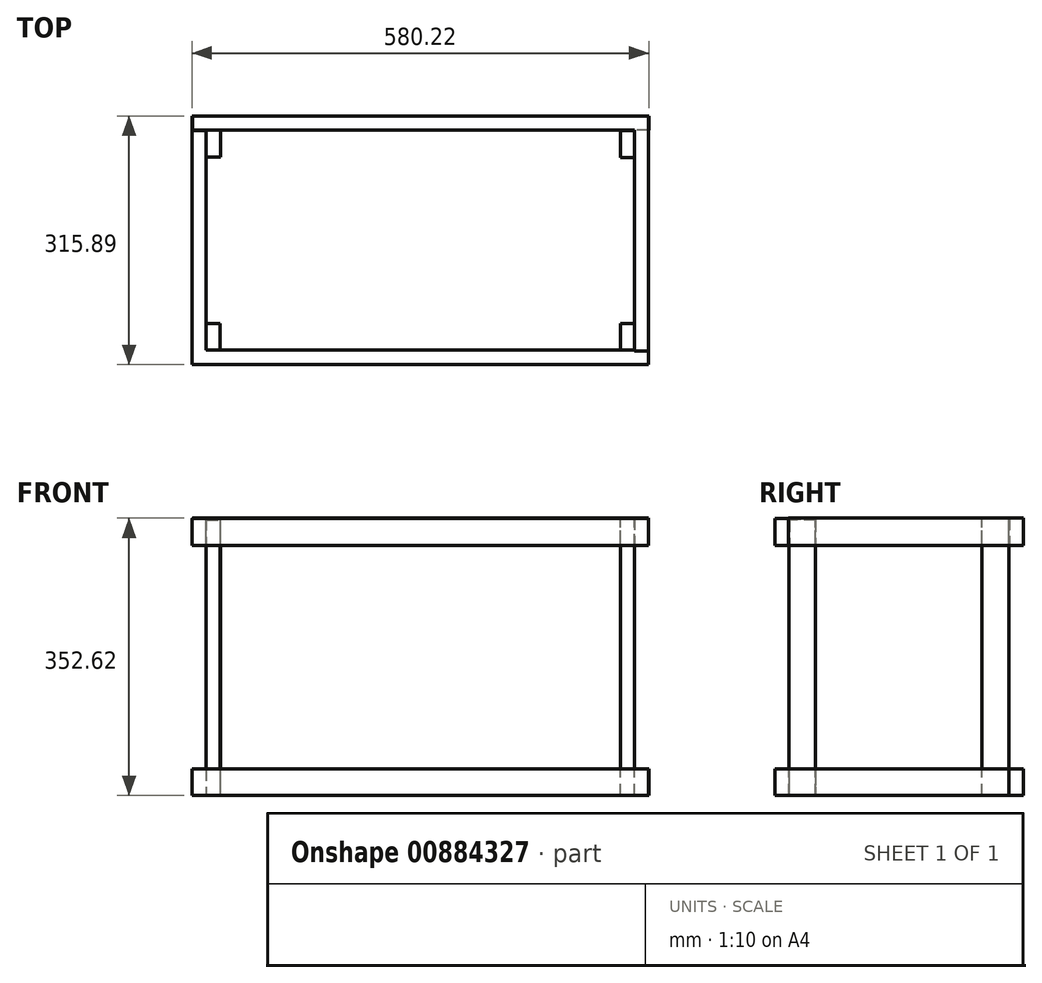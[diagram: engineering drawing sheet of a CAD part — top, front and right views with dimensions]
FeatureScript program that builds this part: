
annotation { "Feature Type Name" : "Feature", "Feature Type Description" : "" }
export const myFeature = defineFeature(function(context is Context, id is Id, definition is map)
    precondition{}
    {
        {
            var Q0;
            Q0=qCreatedBy(makeId("Top.planeOp"),FACE);
            var sketch = newSketch(context, id + "F0", { "sketchPlane" : qUnion([Q0])});
            skLineSegment(sketch, "E0.bottom", {"start": v(0, 0) * mm, "end": v(-18, 0) * mm});
            skLineSegment(sketch, "E0.top", {"start": v(0, -33.75) * mm, "end": v(-18, -33.75) * mm});
            skLineSegment(sketch, "E0.left", {"start": v(0, 0) * mm, "end": v(0, -33.75) * mm});
            skLineSegment(sketch, "E0.right", {"start": v(-18, 0) * mm, "end": v(-18, -33.75) * mm});
            skSolve(sketch);
        }
        {
            var Q0;
            Q0 = qSketchRegion(id + "F0", true);
            extrude(context, id + "F1", {"entities" : qUnion([Q0]), "depth" : 350 * mm, "offsetDistance" : 25.4 * mm});
        }
        {
            var Q0;
            Q0=qCreatedBy(makeId("Top.planeOp"),FACE);
            var sketch = newSketch(context, id + "F2", { "sketchPlane" : qUnion([Q0])});
            skLineSegment(sketch, "E1.bottom", {"start": v(-17.7, -33.83) * mm, "end": v(-35.69, -33.83) * mm});
            skLineSegment(sketch, "E1.top", {"start": v(-17.7, 245.87) * mm, "end": v(-35.69, 245.87) * mm});
            skLineSegment(sketch, "E1.left", {"start": v(-17.7, -33.83) * mm, "end": v(-17.7, 245.87) * mm});
            skLineSegment(sketch, "E1.right", {"start": v(-35.69, -33.83) * mm, "end": v(-35.69, 245.87) * mm});
            skSolve(sketch);
        }
        {
            var Q0;
            Q0 = qSketchRegion(id + "F2", true);
            extrude(context, id + "F3", {"entities" : qUnion([Q0]), "operationType" : NewBodyOperationType.ADD, "depth" : 33.78 * mm, "offsetDistance" : 25.4 * mm});
        }
        {
            var Q0;
            Q0=makeQuery(id+"F3.opExtrude","SWEPT_FACE",FACE,{"disambiguationData":[OSD([sQuery(id+"F2.wireOp",EDGE,"E1.bottom")])]});
            var sketch = newSketch(context, id + "F4", { "sketchPlane" : qUnion([Q0])});
            skPoint(sketch, "E2.oppositeSnap0", {"position": v(-26.7, 33.78) * mm});
            skLineSegment(sketch, "E2.bottom", {"start": v(-35.69, 0) * mm, "end": v(544.25, 0) * mm});
            skLineSegment(sketch, "E2.top", {"start": v(-35.69, 33.78) * mm, "end": v(544.25, 33.78) * mm});
            skLineSegment(sketch, "E2.left", {"start": v(-35.69, 0) * mm, "end": v(-35.69, 33.78) * mm});
            skLineSegment(sketch, "E2.right", {"start": v(544.25, 0) * mm, "end": v(544.25, 33.78) * mm});
            skSolve(sketch);
        }
        {
            var Q0;
            Q0 = qSketchRegion(id + "F4", true);
            extrude(context, id + "F5", {"entities" : qUnion([Q0]), "operationType" : NewBodyOperationType.ADD, "depth" : 18.03 * mm, "offsetDistance" : 25.4 * mm});
        }
        {
            var Q0;
            Q0=makeQuery(id+"F5.opExtrude","CAP_FACE",FACE,{"disambiguationData":[OSD([sQuery(id+"F4.wireOp",EDGE,"E2.bottom"),sQuery(id+"F4.wireOp",EDGE,"E2.top"),sQuery(id+"F4.wireOp",EDGE,"E2.left"),sQuery(id+"F4.wireOp",EDGE,"E2.right")])],"isStart":true});
            var sketch = newSketch(context, id + "F6", { "sketchPlane" : qUnion([Q0])});
            skLineSegment(sketch, "E3.bottom", {"start": v(-544.25, 0) * mm, "end": v(-526.26, 0) * mm});
            skLineSegment(sketch, "E3.top", {"start": v(-544.25, 33.78) * mm, "end": v(-526.26, 33.78) * mm});
            skLineSegment(sketch, "E3.left", {"start": v(-544.25, 0) * mm, "end": v(-544.25, 33.78) * mm});
            skLineSegment(sketch, "E3.right", {"start": v(-526.26, 0) * mm, "end": v(-526.26, 33.78) * mm});
            skSolve(sketch);
        }
        {
            var Q0;
            Q0=makeQuery(id+"F6.imprint","IMPRINT",FACE,{"disambiguationData":[TD([[makeQuery(id+"F6.imprint","IMPRINT",EDGE,{"derivedFrom":sQuery(id+"F6.wireOp",EDGE,"E3.bottom")}),-1.0]])]});
            extrude(context, id + "F7", {"entities" : qUnion([Q0]), "operationType" : NewBodyOperationType.ADD, "depth" : 279.9 * mm, "offsetDistance" : 25.4 * mm});
        }
        {
            var Q0;
            Q0=makeQuery(id+"F3.opExtrude","SWEPT_FACE",FACE,{"disambiguationData":[OSD([sQuery(id+"F2.wireOp",EDGE,"E1.top")])]});
            var sketch = newSketch(context, id + "F8", { "sketchPlane" : qUnion([Q0])});
            skLineSegment(sketch, "E4.bottom", {"start": v(35.69, 0) * mm, "end": v(-544.48, 0) * mm});
            skLineSegment(sketch, "E4.top", {"start": v(35.69, 33.7) * mm, "end": v(-544.48, 33.7) * mm});
            skLineSegment(sketch, "E4.left", {"start": v(35.69, 0) * mm, "end": v(35.69, 33.7) * mm});
            skLineSegment(sketch, "E4.right", {"start": v(-544.48, 0) * mm, "end": v(-544.48, 33.7) * mm});
            skSolve(sketch);
        }
        {
            var Q0;
            Q0 = qSketchRegion(id + "F8", true);
            extrude(context, id + "F9", {"entities" : qUnion([Q0]), "operationType" : NewBodyOperationType.ADD, "depth" : 18.03 * mm, "offsetDistance" : 25.4 * mm});
        }
        {
            var Q0;
            {var subQ1=sQuery(id+"F2.wireOp",EDGE,"E1.left");var subQ4=sQuery(id+"F0.wireOp",EDGE,"E0.bottom");Q0=makeQuery(id+"F3.boolean.opBoolean","SPLIT",FACE,{"disambiguationData":[TD([makeQuery(id+"F1.opExtrude","SWEPT_FACE",FACE,{"disambiguationData":[OSD([subQ4])]})])],"derivedFrom":makeQuery(id+"F3.opExtrude","SWEPT_FACE",FACE,{"disambiguationData":[OSD([subQ1])]})});}
            var sketch = newSketch(context, id + "F10", { "sketchPlane" : qUnion([Q0])});
            skLineSegment(sketch, "E5.bottom", {"start": v(245.87, 0) * mm, "end": v(211.55, 0) * mm});
            skLineSegment(sketch, "E5.top", {"start": v(245.87, 351.9) * mm, "end": v(211.55, 351.9) * mm});
            skLineSegment(sketch, "E5.left", {"start": v(245.87, 0) * mm, "end": v(245.87, 351.9) * mm});
            skLineSegment(sketch, "E5.right", {"start": v(211.55, 0) * mm, "end": v(211.55, 351.9) * mm});
            skSolve(sketch);
        }
        {
            var Q0;
            Q0 = qSketchRegion(id + "F10", true);
            extrude(context, id + "F11", {"entities" : qUnion([Q0]), "operationType" : NewBodyOperationType.ADD, "depth" : 18.03 * mm, "offsetDistance" : 25.4 * mm});
        }
        {
            var Q0;
            Q0=makeQuery(id+"F7.opExtrude","SWEPT_FACE",FACE,{"disambiguationData":[OSD([sQuery(id+"F6.wireOp",EDGE,"E3.right")])]});
            var sketch = newSketch(context, id + "F12", { "sketchPlane" : qUnion([Q0])});
            skLineSegment(sketch, "E6.bottom", {"start": v(33.83, 0) * mm, "end": v(0, 0) * mm});
            skLineSegment(sketch, "E6.top", {"start": v(33.83, 351.49) * mm, "end": v(0, 351.49) * mm});
            skLineSegment(sketch, "E6.left", {"start": v(33.83, 0) * mm, "end": v(33.83, 351.49) * mm});
            skLineSegment(sketch, "E6.right", {"start": v(0, 0) * mm, "end": v(0, 351.49) * mm});
            skSolve(sketch);
        }
        {
            var Q0;
            Q0 = qSketchRegion(id + "F12", true);
            extrude(context, id + "F13", {"entities" : qUnion([Q0]), "operationType" : NewBodyOperationType.ADD, "depth" : 18.03 * mm, "offsetDistance" : 25.4 * mm});
        }
        {
            var Q0;
            {var subQ1=sQuery(id+"F6.wireOp",EDGE,"E3.right");var subQ3=makeQuery(id+"F7.opExtrude","CAP_EDGE",EDGE,{"disambiguationData":[OSD([subQ1])],"isStart":false});Q0=makeQuery(id+"F12.imprint","IMPRINT",FACE,{"disambiguationData":[TD([[makeQuery(id+"F12.imprint","IMPRINT",EDGE,{"derivedFrom":subQ3}),-1.0]])]});}
            var sketch = newSketch(context, id + "F14", { "sketchPlane" : qUnion([Q0])});
            skLineSegment(sketch, "E7.bottom", {"start": v(-245.5, 0) * mm, "end": v(-211.09, 0) * mm});
            skLineSegment(sketch, "E7.top", {"start": v(-245.5, 351.38) * mm, "end": v(-211.09, 351.38) * mm});
            skLineSegment(sketch, "E7.left", {"start": v(-245.5, 0) * mm, "end": v(-245.5, 351.38) * mm});
            skLineSegment(sketch, "E7.right", {"start": v(-211.09, 0) * mm, "end": v(-211.09, 351.38) * mm});
            skSolve(sketch);
        }
        {
            var Q0;
            Q0 = qSketchRegion(id + "F14", true);
            extrude(context, id + "F15", {"entities" : qUnion([Q0]), "operationType" : NewBodyOperationType.ADD, "depth" : 18.03 * mm, "offsetDistance" : 25.4 * mm});
        }
        {
            var Q0;
            {var subQ0=sQuery(id+"F12.wireOp",EDGE,"E6.top");Q0=makeQuery(id+"F12.imprint","IMPRINT",FACE,{"disambiguationData":[TD([[makeQuery(id+"F12.imprint","IMPRINT",EDGE,{"derivedFrom":subQ0}),1.0]])]});}
            var sketch = newSketch(context, id + "F16", { "sketchPlane" : qUnion([Q0])});
            skLineSegment(sketch, "E8.bottom", {"start": v(34.73, 352.62) * mm, "end": v(-246, 352.62) * mm});
            skLineSegment(sketch, "E8.top", {"start": v(34.73, 317.64) * mm, "end": v(-246, 317.64) * mm});
            skLineSegment(sketch, "E8.left", {"start": v(34.73, 352.62) * mm, "end": v(34.73, 317.64) * mm});
            skLineSegment(sketch, "E8.right", {"start": v(-246, 352.62) * mm, "end": v(-246, 317.64) * mm});
            skSolve(sketch);
        }
        {
            var Q0;
            Q0 = qSketchRegion(id + "F16", true);
            extrude(context, id + "F17", {"entities" : qUnion([Q0]), "operationType" : NewBodyOperationType.ADD, "oppositeDirection" : true, "depth" : 18.03 * mm, "offsetDistance" : 25.4 * mm});
        }
        {
            var Q0;
            {var subQ0=sQuery(id+"F10.wireOp",EDGE,"E5.top");Q0=makeQuery(id+"F10.imprint","IMPRINT",FACE,{"disambiguationData":[TD([[makeQuery(id+"F10.imprint","IMPRINT",EDGE,{"derivedFrom":subQ0}),1.0]])]});}
            var sketch = newSketch(context, id + "F18", { "sketchPlane" : qUnion([Q0])});
            skLineSegment(sketch, "E9.bottom", {"start": v(245.56, 352.28) * mm, "end": v(-33.49, 352.28) * mm});
            skLineSegment(sketch, "E9.top", {"start": v(245.56, 317.55) * mm, "end": v(-33.49, 317.55) * mm});
            skLineSegment(sketch, "E9.left", {"start": v(245.56, 352.28) * mm, "end": v(245.56, 317.55) * mm});
            skLineSegment(sketch, "E9.right", {"start": v(-33.49, 352.28) * mm, "end": v(-33.49, 317.55) * mm});
            skSolve(sketch);
        }
        {
            var Q0;
            Q0 = qSketchRegion(id + "F18", true);
            extrude(context, id + "F19", {"entities" : qUnion([Q0]), "operationType" : NewBodyOperationType.ADD, "oppositeDirection" : true, "depth" : 18.03 * mm, "offsetDistance" : 25.4 * mm});
        }
        {
            var Q0;
            Q0=makeQuery(id+"F17.opExtrude","SWEPT_FACE",FACE,{"disambiguationData":[OSD([sQuery(id+"F16.wireOp",EDGE,"E8.right")])]});
            var sketch = newSketch(context, id + "F20", { "sketchPlane" : qUnion([Q0])});
            skLineSegment(sketch, "E10.bottom", {"start": v(-544.3, 317.64) * mm, "end": v(34.82, 317.64) * mm});
            skLineSegment(sketch, "E10.top", {"start": v(-544.3, 352.62) * mm, "end": v(34.82, 352.62) * mm});
            skLineSegment(sketch, "E10.left", {"start": v(-544.3, 317.64) * mm, "end": v(-544.3, 352.62) * mm});
            skLineSegment(sketch, "E10.right", {"start": v(34.82, 317.64) * mm, "end": v(34.82, 352.62) * mm});
            skSolve(sketch);
        }
        {
            var Q0;
            Q0 = qSketchRegion(id + "F20", true);
            extrude(context, id + "F21", {"entities" : qUnion([Q0]), "operationType" : NewBodyOperationType.ADD, "depth" : 18.03 * mm, "offsetDistance" : 25.4 * mm});
        }
        {
            var Q0;
            Q0=makeQuery(id+"F19.opExtrude","SWEPT_FACE",FACE,{"disambiguationData":[OSD([sQuery(id+"F18.wireOp",EDGE,"E9.right")])]});
            var sketch = newSketch(context, id + "F22", { "sketchPlane" : qUnion([Q0])});
            skLineSegment(sketch, "E11.bottom", {"start": v(-35.74, 317.55) * mm, "end": v(544.15, 317.55) * mm});
            skLineSegment(sketch, "E11.top", {"start": v(-35.74, 352.28) * mm, "end": v(544.15, 352.28) * mm});
            skLineSegment(sketch, "E11.left", {"start": v(-35.74, 317.55) * mm, "end": v(-35.74, 352.28) * mm});
            skLineSegment(sketch, "E11.right", {"start": v(544.15, 317.55) * mm, "end": v(544.15, 352.28) * mm});
            skSolve(sketch);
        }
        {
            var Q0;
            Q0 = qSketchRegion(id + "F22", true);
            extrude(context, id + "F23", {"entities" : qUnion([Q0]), "operationType" : NewBodyOperationType.ADD, "depth" : 18.03 * mm, "offsetDistance" : 25.4 * mm});
        }
    });
